# Revit family: QF_ELECTROLUXPROFESSIONAL_1LSN0H_TD6-7_HP
name_source: partatom
category: Attrezzature speciali
units: mm (PartAtom-declared; Revit-internal decimal feet)

## family parameters
Basato su piano di lavoro = No
Condiviso = No
Punto di calcolo locali = No
Quota connettore circolare = Usa diametro
Sempre verticale = Sì
Taglio con vuoti quando caricato = No
Tipo di parte = Normale

## types (21) — shared parameters
Depth Actual = 845 mm  [stored 2.77231 ft]
Height Actual = 1050 mm
Latent Heat Output = 0.0
Length Actual = 600 mm  [stored 1.9685 ft]
Modello = TD6-7
Phase = 1
Produttore = Electrolux Professional
Sensible Heat Output = 0.0
URL = www.electroluxprofessional.com
Watts = 2300 W
zero-valued in all types: Gas KW, Prospetto di default, Steam Pounds per Hour

## per-type parameters (varying)
| type | Cycle | Descrizione | Item Number | Volts | Weight |
| 9871830150 | 50 Hz | TUMBLE DRYER TD6-7 7KG GALVA.DRUM HEAT PUMP 230/50/1N COMPASS PRO 6L80 EU SILVER DO.LEFT DISCON. | 1L828D | 230 V | 109 |
| 9871830066 | 60 Hz | TUMBLE DRYER TD6-7 7KG GALVA.DRUM HEAT PUMP 220/60/1 COMPASS PRO 6G81 EU SILVER DO.LEFT MB DISCON. | 1LSN8Y | 220 V | 131 |
| 9871830135 | 50 Hz | TUMBLE DRYER TD6-7 7KG SST DRUM HEAT PUMP 230/50/1N COMPASS PRO 6A81 SE SILVER DO.LEFT.INS. MB | 1L0GKS | 230 V | 131 |
| 9871830165 | 50 Hz | TUMBLE DRYER TD6-7 7KG SST DRUM HEAT PUMP 200/50/1 COMPASS PRO 6L85 JP SILVER DO.LEFT.INS. ELS-NETW. DISCON. 2.I/O | 1LT60Y | 200 V | 109 |
| 9871830049 | 50 Hz | TUMBLE DRYER TD6-7 7KG GALVA.DRUM HEAT PUMP 230/50/1 COMPASS PRO 6G81 EU SILVER DO.LEFT.INS. ELS-NETW. MB DISCON. | 1LSN65 | 230 V | 131 |
| 9871830024 | 50 Hz | TUMBLE DRYER TD6-7 7KG GALVA.DRUM HEAT PUMP 230/50/1N COMPASS PRO 6G81 EU SILVER DO.LEFT.INS. MB DISCON. | 1L80G5 | 230 V | 131 |
| 9871830004 | 50 Hz | TUMBLE DRYER TD6-7 7KG GALVA.DRUM HEAT PUMP 230/50/1N COMPASS PRO 6G81 EU SILVER DO.LEFT MB DISCON. | 1LSN1X | 230 V | 131 |
| 9871830094 | 50 Hz | TUMBLE DRYER TD6-7 7KG SST DRUM HEAT PUMP 220-230/50/1N COMPASS PRO 6G81 EU SILVER DO.LEFT.INS. MB DISCON. | 1LSNFV | 230 V | 131 |
| 9871830166 | 60 Hz | TUMBLE DRYER TD6-7 7KG SST DRUM HEAT PUMP 200/60/1 COMPASS PRO 6L85 JP SILVER DO.LEFT.INS. ELS-NETW. DISCON. 2.I/O | 1LT60Z | 200 V | 109 |
| 9871830146 | 50 Hz | TUMBLE DRYER TD6-7 7KG GALVA.DRUM HEAT PUMP 230/50/1N COMPASS PRO 6A81 SE SILVER DO.LEFT ELS-NETW. PREP.CB MB 2.I/O | 1LSPHJ | 230 V | 109 |
| 9871830037 | 50 Hz | TUMBLE DRYER TD6-7 7KG GALVA.DRUM HEAT PUMP 230/50/1N COMPASS PRO 6A81 SE SILVER DO.LEFT MB | 1L80H3 | 230 V | 131 |
| 9871830007 | 50 Hz | TUMBLE DRYER TD6-7 7KG GALVA.DRUM HEAT PUMP 230/50/1N COMPASS PRO 6A81 SE SILVER DO.LEFT.INS. MB | 1LSN1Z | 230 V | 131 |
| 9871830161 | 50 Hz | TUMBLE DRYER TD6-7 7KG SST DRUM HEAT PUMP 200/50/1 COMPASS PRO 6G85 JP SILVER DO.LEFT.INS. ELS-NETW. MB DISCON. | 1L0H7L | 200 V | 109 |
| 9871830109 | 50 Hz | TUMBLE DRYER TD6-7 7KG SST DRUM HEAT PUMP 230/50/1N COMPASS PRO 6G81 EU SILVER DO.LEFT MB DISCON. | 1L0FYN | 230 V | 131 |
| 9871830169 | 50 Hz | TUMBLE DRYER TD6-7 7KG SST DRUM HEAT PUMP 230/50/1 COMPASS PRO 6L80 EU SST/SILVER DO.LEFT DISCON. | 1LT659 | 230 V | 109 |
| 9871830050 | 50 Hz | TUMBLE DRYER TD6-7 7KG GALVA.DRUM HEAT PUMP 230/50/1 COMPASS PRO 6G81 EU SILVER DO.LEFT.INS. PREP.CB MB DISCON. 2.I/O | 1L8212 | 230 V | 131 |
| 9871830078 | 60 Hz | TUMBLE DRYER TD6-7 7KG GALVA.DRUM HEAT PUMP 220/60/1 COMPASS PRO 6G81 EU SST/SILVER DO.LEFT MB DISCON. | 1L0ELS | 220 V | 131 |
| 9871830058 | 50 Hz | TUMBLE DRYER TD6-7 7KG GALVA.DRUM HEAT PUMP 220/50/1N COMPASS PRO 6L80 EU SILVER DO.LEFT EXT.PM. DISCON. 2.I/O | 1LSN74 | 220 V | 131 |
| 9871830162 | 60 Hz | TUMBLE DRYER TD6-7 7KG SST DRUM HEAT PUMP 200/60/1 COMPASS PRO 6G85 JP SILVER DO.LEFT.INS. ELS-NETW. MB DISCON. | 1L0H7M | 200 V | 109 |
| 9871830127 | 50 Hz | TUMBLE DRYER TD6-7 7KG GALVA.DRUM HEAT PUMP 230/50/1N COMPASS PRO 6G81 EU SILVER DO.LEFT MB DISCON. | 1L0GAP | 230 V | 131 |
| 9871830093 | 50 Hz | TUMBLE DRYER TD6-7 7KG GALVA.DRUM HEAT PUMP 230/50/1N COMPASS PRO 6A81 EU SILVER DO.LEFT.INS. ELS-NETW. MB DISCON. | 1LSNFT | 230 V | 131 |

note: [stored X ft] marks values corroborated as IEEE doubles in the binary element streams (Revit-internal decimal feet)

## geometry (parser evidence)
native form markers: Blend x10
no freeform markers — native parametric forms only
